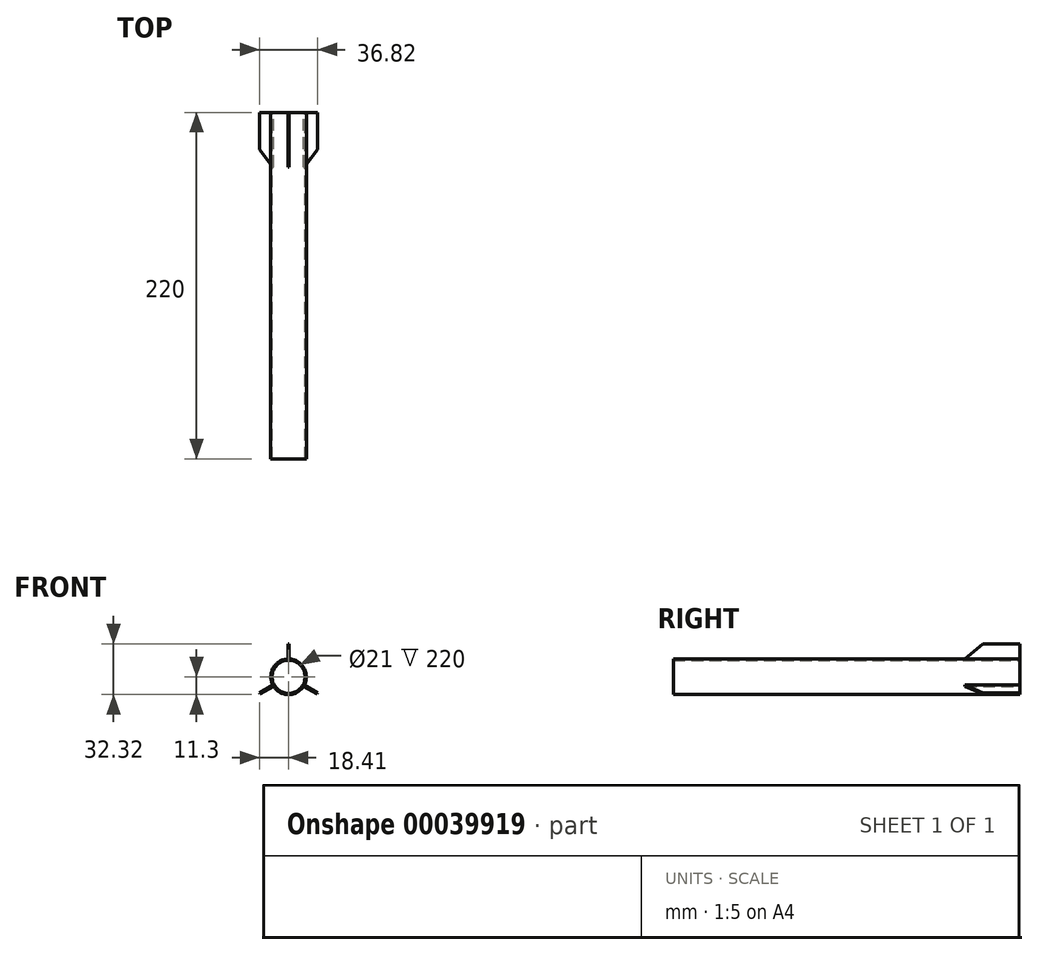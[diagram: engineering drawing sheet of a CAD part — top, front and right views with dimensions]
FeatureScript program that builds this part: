
annotation { "Feature Type Name" : "Feature", "Feature Type Description" : "" }
export const myFeature = defineFeature(function(context is Context, id is Id, definition is map)
    precondition{}
    {
        {
            var Q0;
            Q0=qCreatedBy(makeId("Front.planeOp"),FACE);
            var sketch = newSketch(context, id + "F0", { "sketchPlane" : qUnion([Q0])});
            skCircle(sketch, "E0", {"center": v(0, 0) * mm, "radius": 10.5 * mm});
            skCircle(sketch, "E1", {"center": v(0, 0) * mm, "radius": 11.3 * mm});
            skSolve(sketch);
        }
        {
            var Q0;
            Q0=makeQuery(id+"F0.imprint","IMPRINT",FACE,{"disambiguationData":[TD([[makeQuery(id+"F0.imprint","IMPRINT",EDGE,{"derivedFrom":sQuery(id+"F0.wireOp",EDGE,"E0")}),-1.0]])]});
            var Q1;
            Q1=sQuery(id+"F0.wireOp",EDGE,"E0");
            var Q2;
            Q2=sQuery(id+"F0.wireOp",EDGE,"E1");
            extrude(context, id + "F1", {"entities" : qUnion([Q0]), "surfaceEntities" : qUnion([Q1, Q2]), "depth" : 220 * mm});
        }
        {
            var Q0;
            Q0=qCreatedBy(makeId("Right.planeOp"),FACE);
            var sketch = newSketch(context, id + "F2", { "sketchPlane" : qUnion([Q0])});
            skLineSegment(sketch, "E2", {"start": v(0, 11.01) * mm, "end": v(-35, 11.01) * mm});
            skLineSegment(sketch, "E3", {"start": v(-35, 11.01) * mm, "end": v(-23.52, 21.02) * mm});
            skLineSegment(sketch, "E4", {"start": v(-23.52, 21.02) * mm, "end": v(0, 21.02) * mm});
            skLineSegment(sketch, "E5", {"start": v(0, 21.02) * mm, "end": v(0, 11.01) * mm});
            skSolve(sketch);
        }
        {
            var Q0;
            Q0=makeQuery(id+"F2.imprint","IMPRINT",FACE,{"disambiguationData":[TD([[makeQuery(id+"F2.imprint","IMPRINT",EDGE,{"derivedFrom":sQuery(id+"F2.wireOp",EDGE,"E2")}),-1.0]])]});
            extrude(context, id + "F3", {"entities" : qUnion([Q0]), "endBound" : BoundingType.SYMMETRIC, "depth" : 0.8 * mm});
        }
        {
            var Q0;
            Q0=makeQuery(id+"F3.opExtrude","SWEPT_BODY",BODY,{"disambiguationData":[OSD([sQuery(id+"F2.wireOp",EDGE,"E2"),sQuery(id+"F2.wireOp",EDGE,"E3"),sQuery(id+"F2.wireOp",EDGE,"E4"),sQuery(id+"F2.wireOp",EDGE,"E5")])]});
            var Q1;
            Q1=makeQuery(id+"F1.opExtrude","SWEPT_FACE",FACE,{"disambiguationData":[OSD([sQuery(id+"F0.wireOp",EDGE,"E1")])]});
            circularPattern(context, id + "F4", {"operationType" : NewBodyOperationType.ADD, "entities" : qUnion([Q0]), "axis" : qUnion([Q1]), "angle" : 360 * degree, "instanceCount" : 3, "equalSpace" : true});
        }
    });
